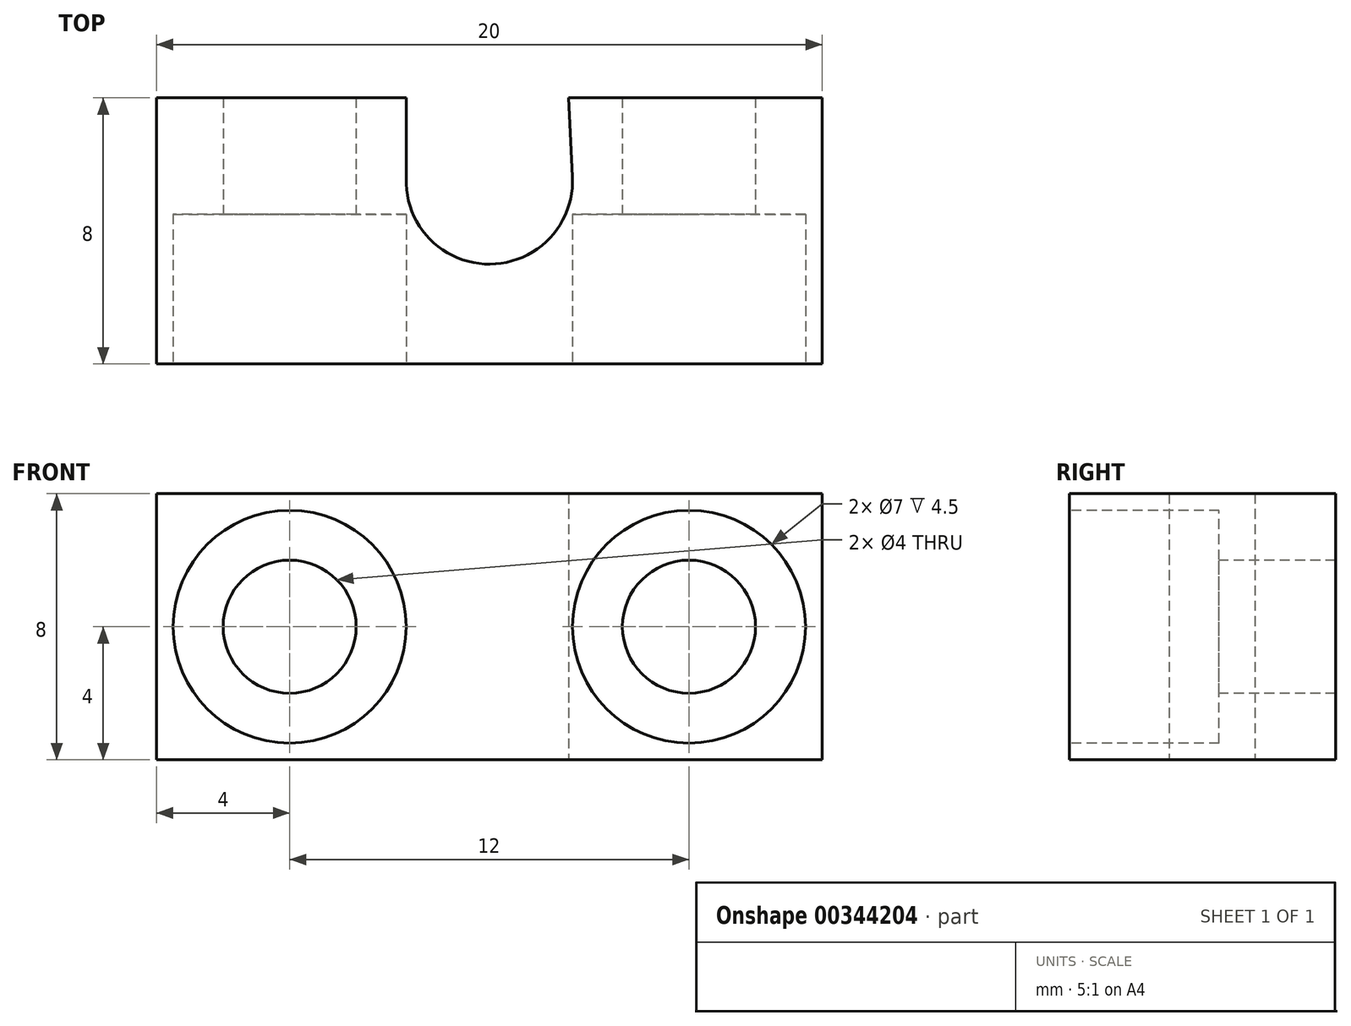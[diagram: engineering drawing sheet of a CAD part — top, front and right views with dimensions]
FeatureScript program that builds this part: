
annotation { "Feature Type Name" : "Feature", "Feature Type Description" : "" }
export const myFeature = defineFeature(function(context is Context, id is Id, definition is map)
    precondition{}
    {
        {
            var Q0;
            Q0=qCreatedBy(makeId("Top.planeOp"),FACE);
            var sketch = newSketch(context, id + "F0", { "sketchPlane" : qUnion([Q0])});
            skLineSegment(sketch, "E0.bottom", {"start": v(-10, 8) * mm, "end": v(-2.5, 8) * mm});
            skLineSegment(sketch, "E0.top", {"start": v(-10, 0) * mm, "end": v(10, 0) * mm});
            skLineSegment(sketch, "E0.left", {"start": v(-10, 8) * mm, "end": v(-10, 0) * mm});
            skLineSegment(sketch, "E0.right", {"start": v(10, 8) * mm, "end": v(10, 0) * mm});
            skArc(sketch, "E1", {"start": v(-2.5, 5.58) * mm, "mid": v(0.02, 3) * mm, "end": v(2.5, 5.62) * mm});
            skLineSegment(sketch, "E2", {"start": v(2.5, 5.62) * mm, "end": v(2.38, 8) * mm});
            skLineSegment(sketch, "E3", {"start": v(-2.5, 5.58) * mm, "end": v(-2.5, 8) * mm});
            skLineSegment(sketch, "E4.trimOffspring", {"start": v(2.38, 8) * mm, "end": v(10, 8) * mm});
            skSolve(sketch);
        }
        {
            var Q0;
            Q0 = qSketchRegion(id + "F0", true);
            extrude(context, id + "F1", {"entities" : qUnion([Q0]), "depth" : 8 * mm});
        }
        {
            var Q0;
            Q0=makeQuery(id+"F1.opExtrude","SWEPT_FACE",FACE,{"disambiguationData":[OSD([sQuery(id+"F0.wireOp",EDGE,"E0.top")])]});
            var sketch = newSketch(context, id + "F2", { "sketchPlane" : qUnion([Q0])});
            skLineSegment(sketch, "E5", {"start": v(-10, 4) * mm, "end": v(10, 4) * mm, "construction": true});
            skCircle(sketch, "E6", {"center": v(6, 4) * mm, "radius": 3.5 * mm});
            skCircle(sketch, "E7", {"center": v(-6, 4) * mm, "radius": 3.5 * mm});
            skSolve(sketch);
        }
        {
            var Q0;
            Q0 = qSketchRegion(id + "F2", true);
            extrude(context, id + "F3", {"entities" : qUnion([Q0]), "operationType" : NewBodyOperationType.REMOVE, "oppositeDirection" : true, "depth" : 4.5 * mm});
        }
        {
            var Q0;
            Q0=makeQuery(id+"F3.boolean.opBoolean","COPY",FACE,{"derivedFrom":makeQuery(id+"F3.opExtrude","CAP_FACE",FACE,{"disambiguationData":[OSD([sQuery(id+"F2.wireOp",EDGE,"E7")])],"isStart":false})});
            var sketch = newSketch(context, id + "F4", { "sketchPlane" : qUnion([Q0])});
            skCircle(sketch, "E8", {"center": v(-6, 4) * mm, "radius": 2 * mm});
            skSolve(sketch);
        }
        {
            var Q0;
            Q0=makeQuery(id+"F3.boolean.opBoolean","COPY",FACE,{"derivedFrom":makeQuery(id+"F3.opExtrude","CAP_FACE",FACE,{"disambiguationData":[OSD([sQuery(id+"F2.wireOp",EDGE,"E6")])],"isStart":false})});
            var sketch = newSketch(context, id + "F5", { "sketchPlane" : qUnion([Q0])});
            skCircle(sketch, "E9", {"center": v(6, 4) * mm, "radius": 2 * mm});
            skSolve(sketch);
        }
        {
            var Q0;
            Q0 = qSketchRegion(id + "F4", true);
            var Q1;
            Q1 = qSketchRegion(id + "F5", true);
            extrude(context, id + "F6", {"entities" : qUnion([Q0, Q1]), "operationType" : NewBodyOperationType.REMOVE, "oppositeDirection" : true, "depth" : 25 * mm});
        }
    });
